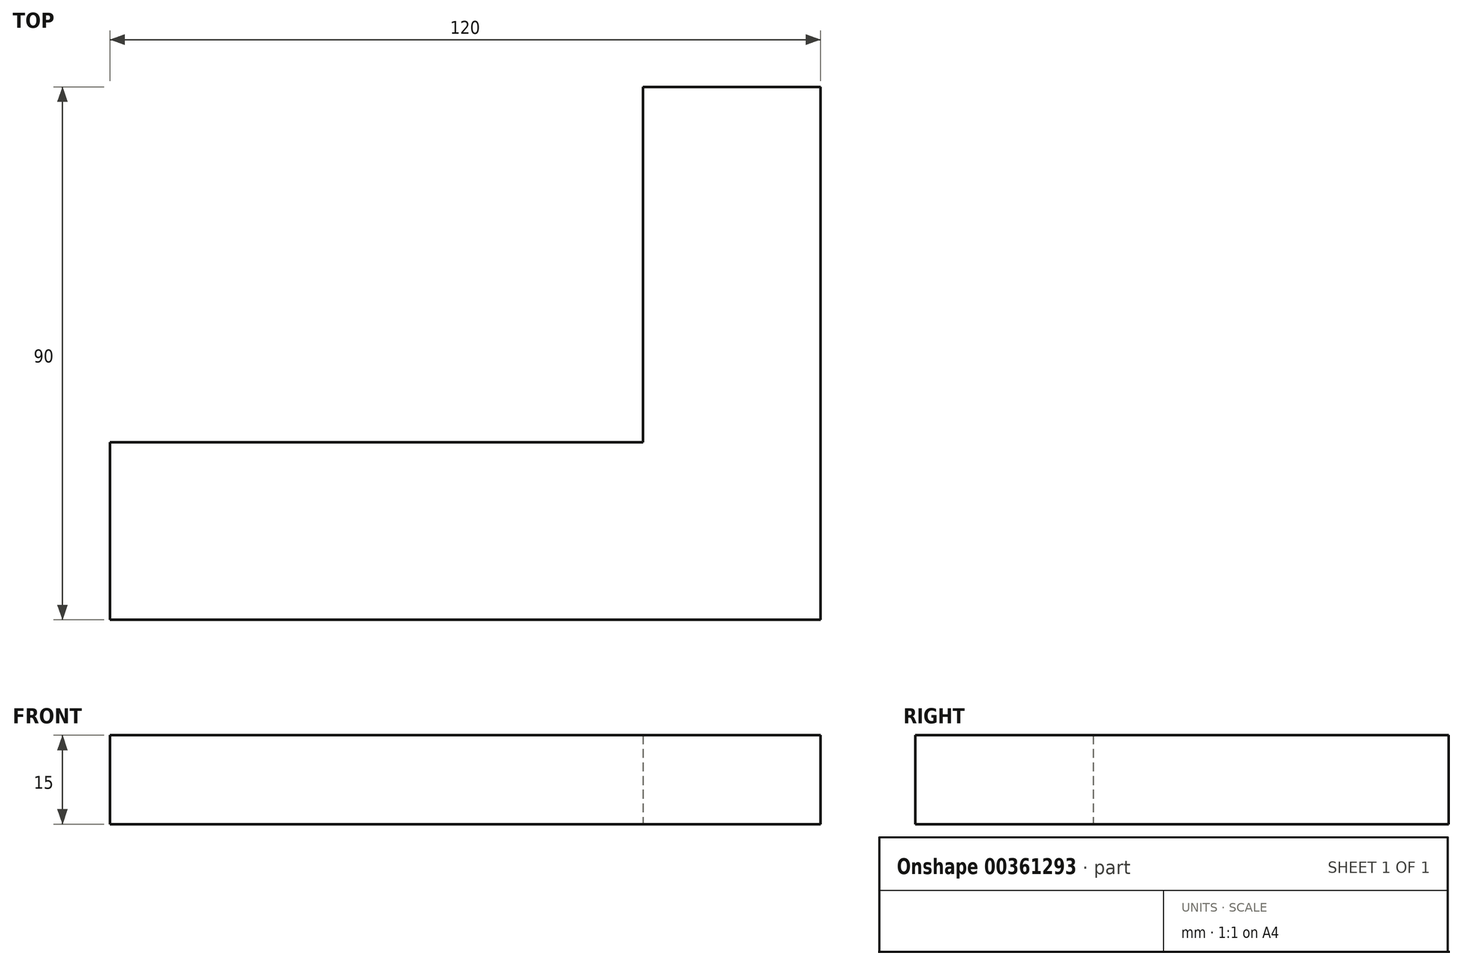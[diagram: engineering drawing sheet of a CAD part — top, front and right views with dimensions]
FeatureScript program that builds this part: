
annotation { "Feature Type Name" : "Feature", "Feature Type Description" : "" }
export const myFeature = defineFeature(function(context is Context, id is Id, definition is map)
    precondition{}
    {
        {
            var Q0;
            Q0=qCreatedBy(makeId("Top.planeOp"),FACE);
            var sketch = newSketch(context, id + "F0", { "sketchPlane" : qUnion([Q0])});
            skLineSegment(sketch, "E0", {"start": v(0, 0) * mm, "end": v(-120, 0) * mm});
            skLineSegment(sketch, "E1", {"start": v(-120, 0) * mm, "end": v(-120, 30) * mm});
            skLineSegment(sketch, "E2", {"start": v(0, 0) * mm, "end": v(0, 90) * mm});
            skLineSegment(sketch, "E3", {"start": v(0, 90) * mm, "end": v(-30, 90) * mm});
            skLineSegment(sketch, "E4", {"start": v(-30, 90) * mm, "end": v(-30, 30) * mm});
            skLineSegment(sketch, "E5", {"start": v(-30, 30) * mm, "end": v(-120, 30) * mm});
            skSolve(sketch);
        }
        {
            var Q0;
            Q0=makeQuery(id+"F0.imprint","IMPRINT",FACE,{"disambiguationData":[TD([[makeQuery(id+"F0.imprint","IMPRINT",EDGE,{"derivedFrom":sQuery(id+"F0.wireOp",EDGE,"E0")}),-1.0]])]});
            extrude(context, id + "F1", {"entities" : qUnion([Q0]), "depth" : 15 * mm});
        }
    });
